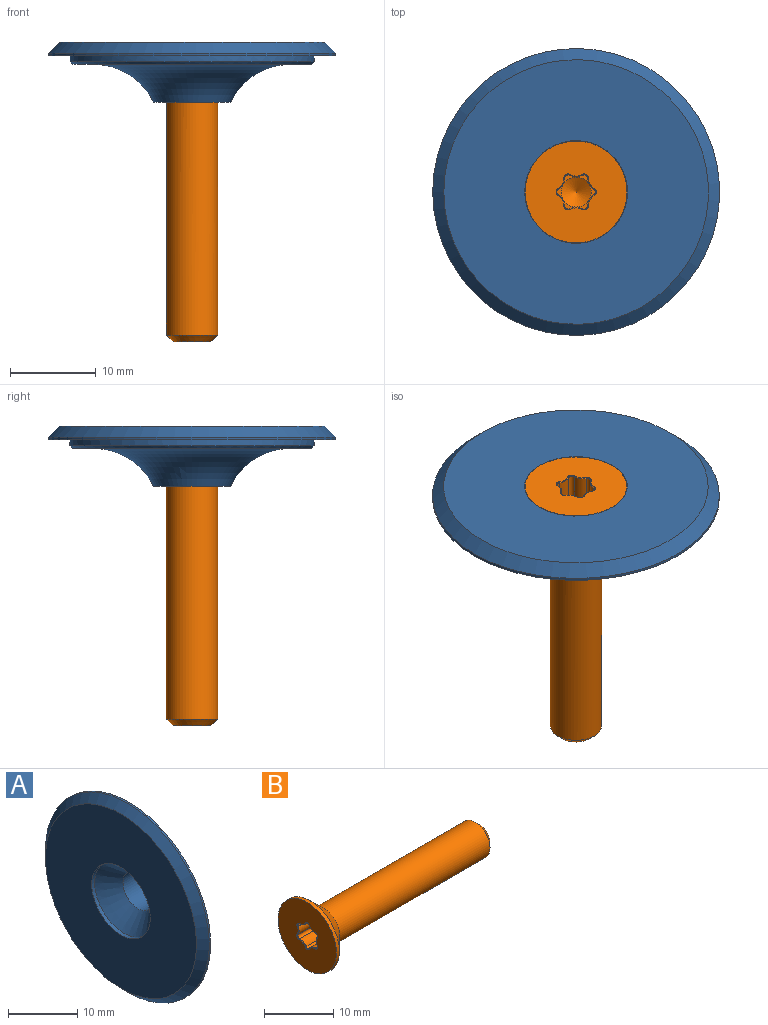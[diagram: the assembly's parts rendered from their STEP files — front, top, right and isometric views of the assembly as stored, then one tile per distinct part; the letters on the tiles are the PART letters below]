
ASSEMBLY  parts=2 mates=1
PART A: 85 faces, bbox 10.4x36.8x36.8 mm
  f0: plane 27.9x27.9mm, normal (1,0,0), area 193.4mm2, adj f6,f11,f12,f13,f14,f15,f16,f17
  f1: plane 30.9x30.9mm, normal (-1,0,0), area 636.8mm2, adj f2,f10
  f2: cylinder r=6mm len=12mm, axis (1,0,0), area 22.6mm2, adj f1,f3
  f3: cone r=6mm half-angle=45deg, axis (-1,0,0), area 117.2mm2, adj f2,f4
  f4: cylinder r=3.1mm len=6.2mm, axis (1,0,0), area 68.2mm2, adj f3,f5
  f5: plane 9x9mm, normal (1,0,0), area 33.4mm2, adj f4,f6
  f6: torus R=11.5mm, axis (1,0,0), area 415.2mm2, adj f0,f5
  f7: cylinder r=14.25mm len=28.5mm, axis (1,0,0), area 62.7mm2, adj f8,f84
  f8: plane 33.5x33.5mm, normal (1,0,0), area 243.5mm2, adj f7,f9
  f9: cylinder r=16.75mm len=33.5mm, axis (1,0,0), area 31.6mm2, adj f8,f10
  f10: cone r=16.75mm half-angle=45deg, axis (1,0,0), area 186mm2, adj f1,f9
  f11: plane 0.15x0.05mm, normal (0,0.19,0.98), area 0mm2, adj f0,f12,f43,f44
  f12: plane 0.12x0.05mm, normal (0,0.31,0.95), area 0mm2, adj f0,f11,f13,f44
  f13: extruded ~0.23x0.05mm, area 0mm2, adj f0,f12,f14,f44
  f14: extruded ~0.25x0.2mm, area 0mm2, adj f0,f13,f15,f44
  f15: extruded ~0.23x0.05mm, area 0mm2, adj f0,f14,f16,f44
  f16: extruded ~0.24x0.2mm, area 0mm2, adj f0,f15,f17,f44
  f17: extruded ~0.25x0.11mm, area 0mm2, adj f0,f16,f18,f44
  f18: extruded ~0.18x0.12mm, area 0mm2, adj f0,f17,f19,f44
  f19: extruded ~0.28x0.06mm, area 0mm2, adj f0,f18,f20,f44
  f20: extruded ~0.29x0.17mm, area 0mm2, adj f0,f19,f21,f44
  f21: extruded ~0.33x0.05mm, area 0mm2, adj f0,f20,f22,f44
  f22: extruded ~0.22x0.18mm, area 0mm2, adj f0,f21,f23,f44
  f23: extruded ~0.21x0.05mm, area 0mm2, adj f0,f22,f24,f44
  f24: extruded ~0.22x0.15mm, area 0mm2, adj f0,f23,f25,f44
  f25: extruded ~0.4x0.31mm, area 0mm2, adj f0,f24,f26,f44
  f26: extruded ~0.32x0.07mm, area 0mm2, adj f0,f25,f43,f44
  f27: extruded ~0.17x0.11mm, area 0mm2, adj f28,f41,f44,f46
  f28: extruded ~0.25x0.08mm, area 0mm2, adj f27,f29,f44,f46
  f29: extruded ~0.23x0.21mm, area 0mm2, adj f28,f30,f44,f46
  f30: extruded ~0.19x0.05mm, area 0mm2, adj f29,f31,f44,f46
  f31: extruded ~0.17x0.13mm, area 0mm2, adj f30,f32,f44,f46
  f32: extruded ~0.25x0.05mm, area 0mm2, adj f31,f33,f44,f46
  f33: extruded ~0.21x0.13mm, area 0mm2, adj f32,f41,f44,f46
  f34: extruded ~0.18x0.11mm, area 0mm2, adj f35,f42,f44,f45
  f35: extruded ~0.18x0.05mm, area 0mm2, adj f34,f36,f44,f45
  f36: extruded ~0.14x0.1mm, area 0mm2, adj f35,f37,f44,f45
  f37: extruded ~0.23x0.08mm, area 0mm2, adj f36,f38,f44,f45
  f38: extruded ~0.19x0.18mm, area 0mm2, adj f37,f39,f44,f45
  f39: extruded ~0.17x0.05mm, area 0mm2, adj f38,f40,f44,f45
  f40: extruded ~0.14x0.11mm, area 0mm2, adj f39,f42,f44,f45
  f41: extruded ~0.21x0.05mm, area 0mm2, adj f27,f33,f44,f46
  f42: extruded ~0.21x0.05mm, area 0mm2, adj f34,f40,f44,f45
  f43: extruded ~0.19x0.15mm, area 0mm2, adj f0,f11,f26,f44
  f44: plane 1.55x1.15mm, normal (1,0,0), area 0.7mm2, adj f11,f12,f13,f14,f15,f16,f17,f18
  f45: plane 0.56x0.53mm, normal (1,0,0), area 0.2mm2, adj f34,f35,f36,f37,f38,f39,f40,f42
  f46: plane 0.66x0.61mm, normal (1,0,0), area 0.3mm2, adj f27,f28,f29,f30,f31,f32,f33,f41
  f47: plane 0.11x0.05mm, normal (0,0.06,1), area 0mm2, adj f0,f48,f73,f74
  f48: plane 0.13x0.05mm, normal (0,0.19,0.98), area 0mm2, adj f0,f47,f49,f74
  f49: extruded ~0.23x0.09mm, area 0mm2, adj f0,f48,f50,f74
  f50: extruded ~0.35x0.17mm, area 0mm2, adj f0,f49,f51,f74
  f51: extruded ~0.34x0.08mm, area 0mm2, adj f0,f50,f52,f74
  f52: extruded ~0.3x0.16mm, area 0mm2, adj f0,f51,f53,f74
  f53: extruded ~0.37x0.13mm, area 0mm2, adj f0,f52,f54,f74
  f54: plane 0.05x0.01mm, normal (0,-0.13,-0.99), area 0mm2, adj f0,f53,f55,f74
  f55: extruded ~0.45x0.2mm, area 0mm2, adj f0,f54,f56,f74
  f56: extruded ~0.38x0.11mm, area 0mm2, adj f0,f55,f57,f74
  f57: extruded ~0.17x0.05mm, area 0mm2, adj f0,f56,f58,f74
  f58: plane 0.14x0.05mm, normal (0,-0.99,0.13), area 0mm2, adj f0,f57,f59,f74
  f59: extruded ~0.18x0.05mm, area 0mm2, adj f0,f58,f60,f74
  f60: extruded ~0.53x0.16mm, area 0mm2, adj f0,f59,f61,f74
  f61: extruded ~0.63x0.25mm, area 0mm2, adj f0,f60,f62,f74
  f62: extruded ~0.5x0.08mm, area 0mm2, adj f0,f61,f73,f74
  f63: extruded ~0.16x0.07mm, area 0mm2, adj f64,f72,f74,f75
  f64: extruded ~0.16x0.1mm, area 0mm2, adj f63,f65,f74,f75
  f65: extruded ~0.2x0.05mm, area 0mm2, adj f64,f66,f74,f75
  f66: extruded ~0.13x0.06mm, area 0mm2, adj f65,f67,f74,f75
  f67: extruded ~0.13x0.09mm, area 0mm2, adj f66,f68,f74,f75
  f68: extruded ~0.17x0.05mm, area 0mm2, adj f67,f69,f74,f75
  f69: extruded ~0.21x0.11mm, area 0mm2, adj f68,f70,f74,f75
  f70: extruded ~0.24x0.05mm, area 0mm2, adj f69,f71,f74,f75
  f71: extruded ~0.25x0.11mm, area 0mm2, adj f70,f72,f74,f75
  f72: extruded ~0.23x0.07mm, area 0mm2, adj f63,f71,f74,f75
  f73: extruded ~0.22x0.19mm, area 0mm2, adj f0,f47,f62,f74
  f74: plane 1.54x0.99mm, normal (1,0,0), area 0.6mm2, adj f47,f48,f49,f50,f51,f52,f53,f54
  f75: plane 0.68x0.64mm, normal (1,0,0), area 0.3mm2, adj f63,f64,f65,f66,f67,f68,f69,f70
  f76: plane 0.19x0.05mm, normal (0,0,1), area 0mm2, adj f0,f77,f82,f83
  f77: plane 1.35x0.61mm, normal (0,-0.91,0.41), area 0.1mm2, adj f0,f76,f78,f83
  f78: plane 0.14x0.05mm, normal (0,-1,0), area 0mm2, adj f0,f77,f79,f83
  f79: plane 0.99x0.05mm, normal (0,0,-1), area 0mm2, adj f0,f78,f80,f83
  f80: plane 0.16x0.05mm, normal (0,1,0), area 0mm2, adj f0,f79,f81,f83
  f81: plane 0.81x0.05mm, normal (0,0,1), area 0mm2, adj f0,f80,f82,f83
  f82: plane 1.33x0.62mm, normal (0,0.91,-0.42), area 0.1mm2, adj f0,f76,f81,f83
  f83: plane 1.49x0.99mm, normal (1,0,0), area 0.4mm2, adj f76,f77,f78,f79,f80,f81,f82
  f84: cone r=13.95mm half-angle=45deg, axis (-1,0,0), area 37.6mm2, adj f0,f7
PART B: 32 faces, bbox 35x11.9x11.9 mm
  f0: plane 11.9x11.9mm, normal (-1,0,0), area 97.6mm2, adj f4,f20,f21,f22,f23,f24,f25,f26
  f1: plane 4.4x4.4mm, normal (1,0,0), area 15.2mm2, adj f5
  f2: cylinder r=3mm len=30.65mm, axis (1,0,0), area 577.7mm2, adj f3,f5
  f3: cone r=5.95mm half-angle=45deg, axis (-1,0,0), area 117.3mm2, adj f2,f4
  f4: cylinder r=5.95mm len=11.9mm, axis (1,0,0), area 22.4mm2, adj f0,f3
  f5: cone r=2.2mm half-angle=45deg, axis (-1,0,0), area 18.5mm2, adj f1,f2
  f6: cylinder r=1.44mm len=3.9mm, axis (-1,0,0), area 5.9mm2, adj f7,f17,f18,f24
  f7: cylinder r=0.41mm len=3.9mm, axis (-1,0,0), area 3.3mm2, adj f6,f8,f18,f26
  f8: cylinder r=1.44mm len=3.9mm, axis (-1,0,0), area 5.9mm2, adj f7,f9,f18,f28
  f9: cylinder r=0.41mm len=3.9mm, axis (-1,0,0), area 3.3mm2, adj f8,f10,f18,f30
  f10: cylinder r=1.44mm len=3.9mm, axis (-1,0,0), area 5.9mm2, adj f9,f11,f18,f31
  f11: cylinder r=0.41mm len=3.9mm, axis (-1,0,0), area 3.3mm2, adj f10,f12,f18,f29
  f12: cylinder r=1.44mm len=3.9mm, axis (-1,0,0), area 5.9mm2, adj f11,f13,f18,f27
  f13: cylinder r=0.41mm len=3.9mm, axis (-1,0,0), area 3.3mm2, adj f12,f14,f18,f25
  f14: cylinder r=1.44mm len=3.9mm, axis (-1,0,0), area 5.9mm2, adj f13,f15,f18,f23
  f15: cylinder r=0.41mm len=3.9mm, axis (-1,0,0), area 3.3mm2, adj f14,f16,f18,f21
  f16: cylinder r=1.44mm len=3.9mm, axis (-1,0,0), area 5.9mm2, adj f15,f17,f18,f20
  f17: cylinder r=0.41mm len=3.9mm, axis (-1,0,0), area 3.3mm2, adj f6,f16,f18,f22
  f18: plane 4.5x4.01mm, normal (-1,0,0), area 2.6mm2, adj f6,f7,f8,f9,f10,f11,f12,f13
  f19: cone r=1.75mm half-angle=59deg, axis (-1,0,0), area 11.2mm2, adj f18
  f20: cone r=1.34mm half-angle=45deg, axis (1,0,0), area 0.2mm2, adj f0,f16,f21,f22
  f21: cone r=0.41mm half-angle=45deg, axis (-1,0,0), area 0.1mm2, adj f0,f15,f20,f23
  f22: cone r=0.41mm half-angle=45deg, axis (-1,0,0), area 0.1mm2, adj f0,f17,f20,f24
  f23: cone r=1.34mm half-angle=45deg, axis (1,0,0), area 0.2mm2, adj f0,f14,f21,f25
  f24: cone r=1.34mm half-angle=45deg, axis (1,0,0), area 0.2mm2, adj f0,f6,f22,f26
  f25: cone r=0.41mm half-angle=45deg, axis (-1,0,0), area 0.1mm2, adj f0,f13,f23,f27
  f26: cone r=0.41mm half-angle=45deg, axis (-1,0,0), area 0.1mm2, adj f0,f7,f24,f28
  f27: cone r=1.34mm half-angle=45deg, axis (1,0,0), area 0.2mm2, adj f0,f12,f25,f29
  f28: cone r=1.34mm half-angle=45deg, axis (1,0,0), area 0.2mm2, adj f0,f8,f26,f30
  f29: cone r=0.41mm half-angle=45deg, axis (-1,0,0), area 0.1mm2, adj f0,f11,f27,f31
  f30: cone r=0.41mm half-angle=45deg, axis (-1,0,0), area 0.1mm2, adj f0,f9,f28,f31
  f31: cone r=1.34mm half-angle=45deg, axis (1,0,0), area 0.2mm2, adj f0,f10,f29,f30
PLACE A rot(axis=(-0.58,0.58,0.58),120deg) t=(0,0,0.1)mm
PLACE B rot(axis=(0,1,0),90deg) t=(0,0,7.1)mm
MATE revolute B.f2 <-> A.f3  axis (0,0,1) through (0,0,7.1)mm
